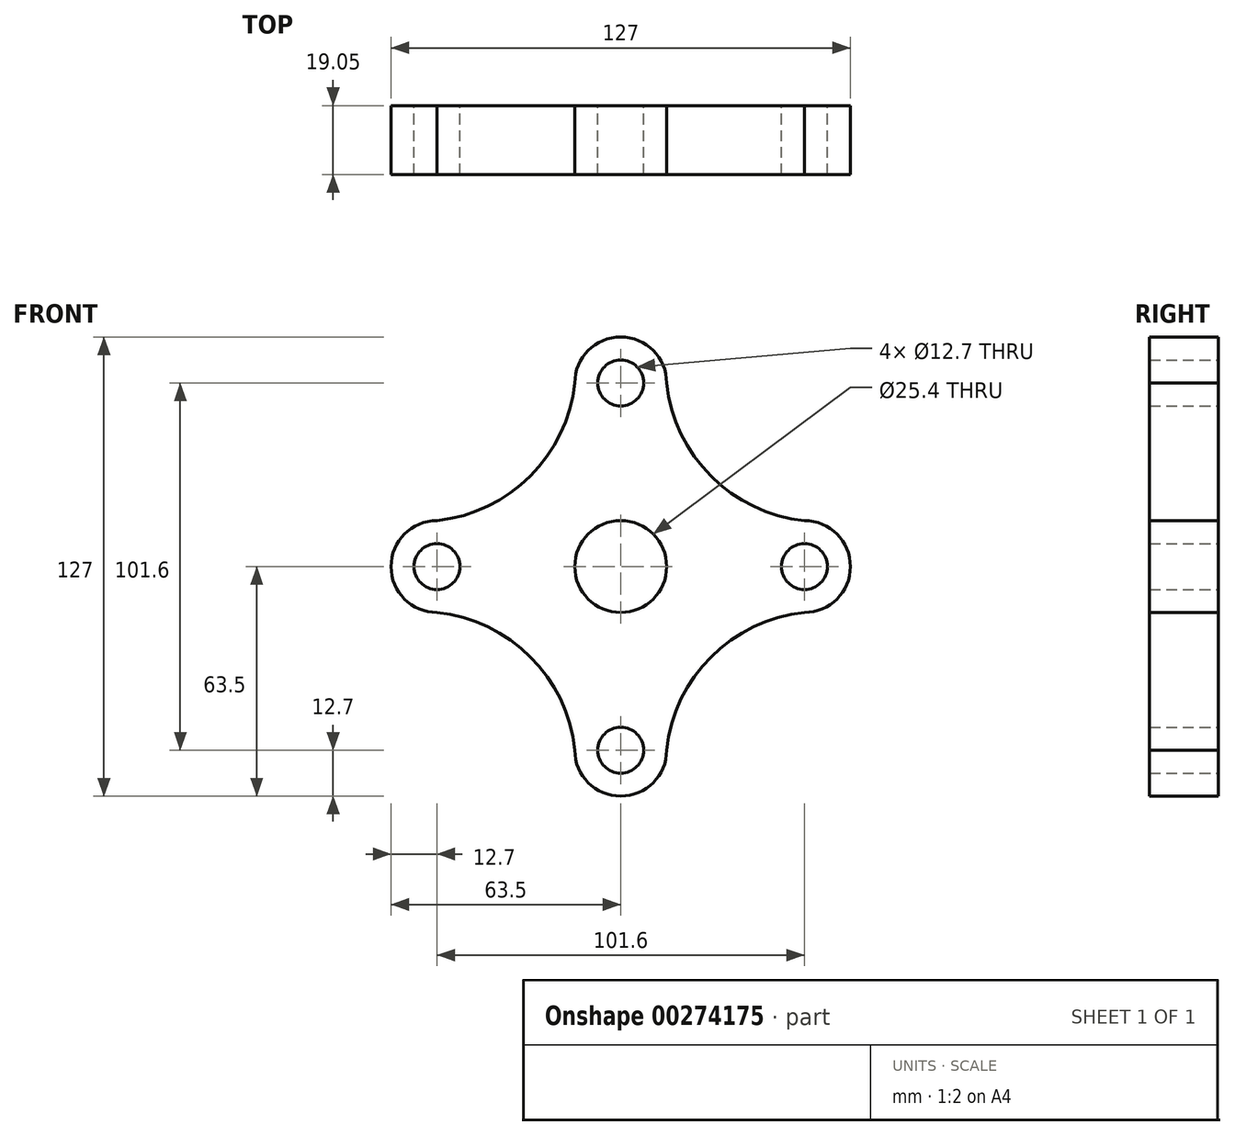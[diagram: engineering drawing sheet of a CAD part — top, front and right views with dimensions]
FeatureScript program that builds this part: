
annotation { "Feature Type Name" : "Feature", "Feature Type Description" : "" }
export const myFeature = defineFeature(function(context is Context, id is Id, definition is map)
    precondition{}
    {
        {
            var Q0;
            Q0=qCreatedBy(makeId("Front.planeOp"),FACE);
            var sketch = newSketch(context, id + "F0", { "sketchPlane" : qUnion([Q0])});
            skCircle(sketch, "E0", {"center": v(-101.6, 50.8) * mm, "radius": 6.35 * mm});
            skCircle(sketch, "E1", {"center": v(0, 50.8) * mm, "radius": 6.35 * mm});
            skCircle(sketch, "E2", {"center": v(-50.8, 50.8) * mm, "radius": 12.7 * mm});
            skCircle(sketch, "E3", {"center": v(-50.8, 0) * mm, "radius": 6.35 * mm});
            skCircle(sketch, "E4", {"center": v(-50.8, 101.6) * mm, "radius": 6.35 * mm});
            skArc(sketch, "E5", {"start": v(-101.6, 63.5) * mm, "mid": v(-75.83, 75.83) * mm, "end": v(-63.5, 101.6) * mm});
            skArc(sketch, "E6", {"start": v(-38.1, 101.6) * mm, "mid": v(-50.8, 114.3) * mm, "end": v(-63.5, 101.6) * mm});
            skArc(sketch, "E7", {"start": v(-101.6, 63.5) * mm, "mid": v(-114.3, 50.8) * mm, "end": v(-101.6, 38.1) * mm});
            skPoint(sketch, "E8.trimOffspring.end.orphan", {"position": v(-101.6, 101.6) * mm});
            skArc(sketch, "E9", {"start": v(-38.1, 101.6) * mm, "mid": v(-25.82, 75.78) * mm, "end": v(0, 63.5) * mm});
            skArc(sketch, "E10", {"start": v(0, 38.1) * mm, "mid": v(12.7, 50.8) * mm, "end": v(0, 63.5) * mm});
            skPoint(sketch, "E11.orphan", {"position": v(0, 101.6) * mm});
            skArc(sketch, "E12", {"start": v(0, 38.1) * mm, "mid": v(-25.82, 25.82) * mm, "end": v(-38.1, 0) * mm});
            skArc(sketch, "E13", {"start": v(-63.5, 0) * mm, "mid": v(-50.8, -12.7) * mm, "end": v(-38.1, 0) * mm});
            skArc(sketch, "E14", {"start": v(-63.5, 0) * mm, "mid": v(-75.78, 25.82) * mm, "end": v(-101.6, 38.1) * mm});
            skPoint(sketch, "E15.orphan", {"position": v(-101.6, 0) * mm});
            skPoint(sketch, "E16.orphan", {"position": v(0, 0) * mm});
            skSolve(sketch);
        }
        {
            var Q0;
            Q0 = qSketchRegion(id + "F0", true);
            extrude(context, id + "F1", {"entities" : qUnion([Q0]), "depth" : 19.05 * mm});
        }
    });
